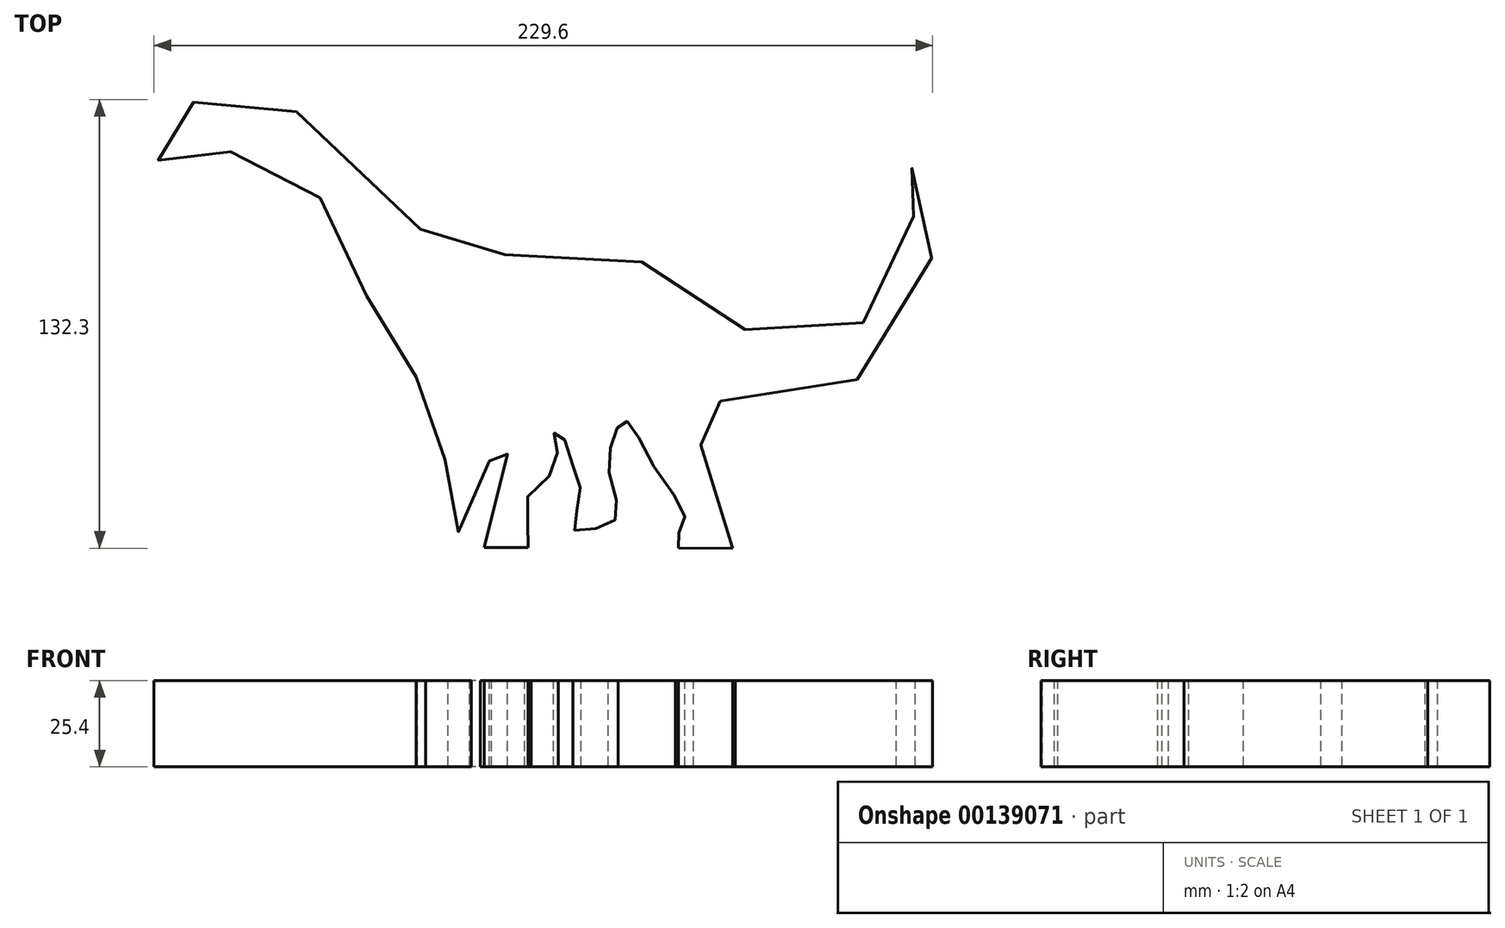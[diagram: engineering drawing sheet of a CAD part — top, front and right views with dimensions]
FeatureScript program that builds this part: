
annotation { "Feature Type Name" : "Feature", "Feature Type Description" : "" }
export const myFeature = defineFeature(function(context is Context, id is Id, definition is map)
    precondition{}
    {
        {
            var Q0;
            Q0=qCreatedBy(makeId("Top.planeOp"),FACE);
            var sketch = newSketch(context, id + "F0", { "sketchPlane" : qUnion([Q0])});
            skFitSpline(sketch, "E0", {"points": [v(-110.43, 35.92) * mm, v(-92.04, 35.13) * mm, v(-66.55, 22.78) * mm, v(-34.5, -13.22) * mm, v(-29.5, -12.16) * mm, v(0, -7.43) * mm, v(25.68, -14.53) * mm, v(46.7, -29.24) * mm, v(69.56, -36.34) * mm, v(93.74, -21.62) * mm, v(100.57, 0) * mm, v(95.31, 16.21) * mm, v(95.58, 17.8) * mm, v(99.26, 16.48) * mm, v(104.77, 2.29) * mm, v(105.56, -10.85) * mm, v(91.37, -40.8) * mm, v(52.48, -53.94) * mm, v(39.08, -52.9) * mm, v(35.4, -57.36) * mm, v(37.24, -63.4) * mm, v(38.82, -73.65) * mm, v(46.95, -96.1) * mm, v(30.84, -96.05) * mm, v(30.94, -91.78) * mm, v(32.78, -86.53) * mm, v(24.37, -73.13) * mm, v(16.75, -59.46) * mm, v(14.38, -58.67) * mm, v(11.75, -63.4) * mm, v(10.44, -73.65) * mm, v(13.04, -86.05) * mm, v(7.96, -89.87) * mm, v(0, -90.47) * mm, v(2.03, -81.27) * mm, v(0, -72.34) * mm, v(-4.01, -62.09) * mm, v(-5.85, -62.35) * mm, v(-4.8, -71.29) * mm, v(-14.26, -82.32) * mm, v(-12.95, -95.2) * mm, v(-24.5, -97.83) * mm, v(-26.35, -85.21) * mm, v(-19.52, -69.7) * mm, v(-23.46, -60.51) * mm, v(-24.77, -61.56) * mm, v(-24.5, -69.45) * mm, v(-30.55, -78.12) * mm, v(-31.08, -89.15) * mm, v(-42.64, -90.73) * mm, v(-38.43, -71.29) * mm, v(-38.17, -60.78) * mm, v(-46.32, -46.32) * mm, v(-46.32, -39.75) * mm, v(-60.5, -22.41) * mm, v(-68.92, -4.28) * mm, v(-78.9, 12.01) * mm, v(-95.98, 20.42) * mm, v(-104.91, 20.16) * mm, v(-107.02, 18.58) * mm, v(-122, 18.05) * mm, v(-123.05, 23.57) * mm, v(-114.64, 33.82) * mm, v(-110.43, 35.92) * mm]});
            skFitSpline(sketch, "E1", {"points": [v(473.58, 95.33) * mm, v(157.06, 91.37) * mm], "startDerivative": vector(2.75, 4.19) * mm, "endDerivative": vector(2.75, 4.19) * mm});
            skLineSegment(sketch, "E2", {"start": v(-52.22, -95.8) * mm, "end": v(89.32, -96.22) * mm});
            skSolve(sketch);
        }
        {
            var Q0;
            {var subQ0=sQuery(id+"F0.wireOp",EDGE,"E2");var subQ1=sQuery(id+"F0.wireOp",EDGE,"E0");var subQ2=makeQuery(id+"F0.imprint","INTERSECT",VERTEX,{"disambiguationData":[OD(2.0)],"derivedFrom":[subQ1,subQ0]});Q0=makeQuery(id+"F0.imprint","IMPRINT",FACE,{"disambiguationData":[TD([[makeQuery(id+"F0.imprint","IMPRINT",EDGE,{"disambiguationData":[TD([[subQ2,-1.0]])],"derivedFrom":subQ1}),-1.0]])]});}
            extrude(context, id + "F1", {"entities" : qUnion([Q0]), "depth" : 25.4 * mm});
        }
    });
